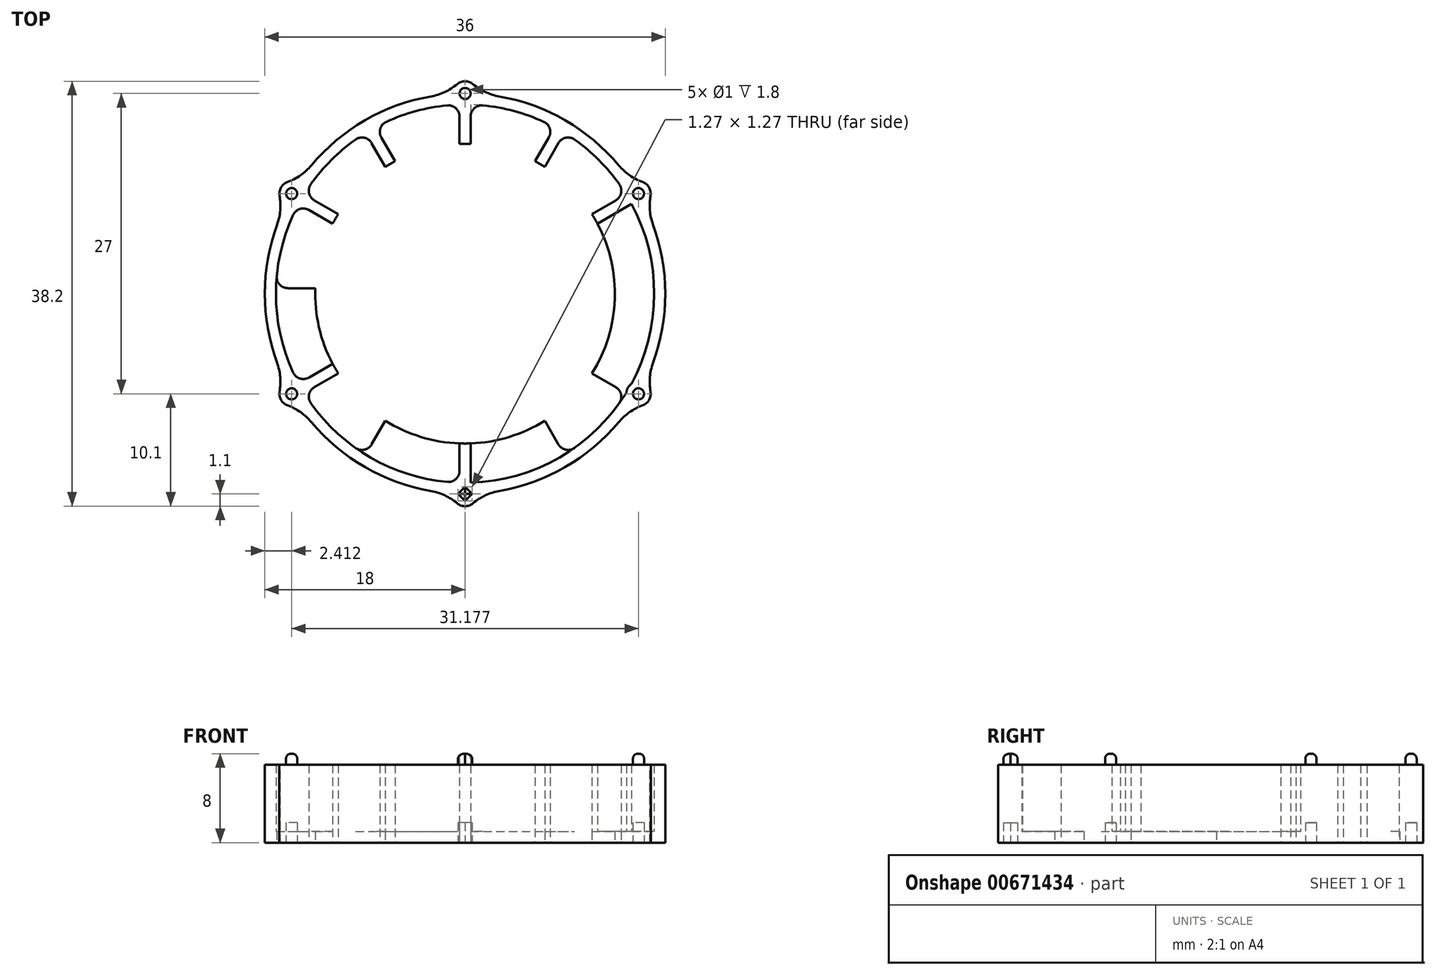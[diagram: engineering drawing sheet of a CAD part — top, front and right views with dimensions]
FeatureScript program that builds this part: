
annotation { "Feature Type Name" : "Feature", "Feature Type Description" : "" }
export const myFeature = defineFeature(function(context is Context, id is Id, definition is map)
    precondition{}
    {
        {
            var Q0;
            Q0=qCreatedBy(makeId("Top.planeOp"),FACE);
            var sketch = newSketch(context, id + "F0", { "sketchPlane" : qUnion([Q0])});
            skCircle(sketch, "E0", {"center": v(0, 0) * mm, "radius": 18 * mm});
            skCircle(sketch, "E1.0", {"center": v(0, 0) * mm, "radius": 17 * mm});
            skLineSegment(sketch, "E2.bottom", {"start": v(8.56, 15.83) * mm, "end": v(9.43, 15.33) * mm});
            skLineSegment(sketch, "E2.top", {"start": v(-9.43, -15.33) * mm, "end": v(-8.56, -15.83) * mm});
            skLineSegment(sketch, "E2.left", {"start": v(8.56, 15.83) * mm, "end": v(-9.43, -15.33) * mm});
            skLineSegment(sketch, "E2.right", {"start": v(9.43, 15.33) * mm, "end": v(-8.56, -15.83) * mm});
            skLineSegment(sketch, "E3.bottom", {"start": v(15.33, 9.43) * mm, "end": v(15.83, 8.56) * mm});
            skLineSegment(sketch, "E3.top", {"start": v(-15.83, -8.56) * mm, "end": v(-15.33, -9.43) * mm});
            skLineSegment(sketch, "E3.left", {"start": v(15.33, 9.43) * mm, "end": v(-15.83, -8.56) * mm});
            skLineSegment(sketch, "E3.right", {"start": v(15.83, 8.56) * mm, "end": v(-15.33, -9.43) * mm});
            skLineSegment(sketch, "E4", {"start": v(-38.35, 0) * mm, "end": v(39.17, 0) * mm, "construction": true});
            skLineSegment(sketch, "E5", {"start": v(0, 42.5) * mm, "end": v(0, -42.47) * mm, "construction": true});
            skLineSegment(sketch, "E6.bottom", {"start": v(-18, 0.5) * mm, "end": v(18, 0.5) * mm});
            skLineSegment(sketch, "E6.top", {"start": v(-18, -0.5) * mm, "end": v(18, -0.5) * mm});
            skLineSegment(sketch, "E6.left", {"start": v(-18, 0.5) * mm, "end": v(-18, -0.5) * mm});
            skLineSegment(sketch, "E6.right", {"start": v(18, 0.5) * mm, "end": v(18, -0.5) * mm});
            skLineSegment(sketch, "E7.bottom", {"start": v(-15.33, 9.43) * mm, "end": v(15.83, -8.56) * mm});
            skLineSegment(sketch, "E7.top", {"start": v(-15.83, 8.56) * mm, "end": v(15.33, -9.43) * mm});
            skLineSegment(sketch, "E7.left", {"start": v(-15.33, 9.43) * mm, "end": v(-15.83, 8.56) * mm});
            skLineSegment(sketch, "E7.right", {"start": v(15.83, -8.56) * mm, "end": v(15.33, -9.43) * mm});
            skLineSegment(sketch, "E8.bottom", {"start": v(-0.5, 18) * mm, "end": v(0.5, 18) * mm});
            skLineSegment(sketch, "E8.top", {"start": v(-0.5, -18) * mm, "end": v(0.5, -18) * mm});
            skLineSegment(sketch, "E8.left", {"start": v(-0.5, 18) * mm, "end": v(-0.5, -18) * mm});
            skLineSegment(sketch, "E8.right", {"start": v(0.5, 18) * mm, "end": v(0.5, -18) * mm});
            skLineSegment(sketch, "E9.bottom", {"start": v(-9.43, 15.33) * mm, "end": v(-8.56, 15.83) * mm});
            skLineSegment(sketch, "E9.top", {"start": v(8.56, -15.83) * mm, "end": v(9.43, -15.33) * mm});
            skLineSegment(sketch, "E9.left", {"start": v(-9.43, 15.33) * mm, "end": v(8.56, -15.83) * mm});
            skLineSegment(sketch, "E9.right", {"start": v(-8.56, 15.83) * mm, "end": v(9.43, -15.33) * mm});
            skCircle(sketch, "E10", {"center": v(0, 0) * mm, "radius": 13.47 * mm});
            skSolve(sketch);
        }
        {
            var Q0;
            Q0=qCreatedBy(makeId("Top.planeOp"),FACE);
            var sketch = newSketch(context, id + "F1", { "sketchPlane" : qUnion([Q0])});
            skCircle(sketch, "E11", {"center": v(0, 0) * mm, "radius": 18 * mm});
            skCircle(sketch, "E12", {"center": v(0, 0) * mm, "radius": 17 * mm});
            skSolve(sketch);
        }
        {
            var Q0;
            Q0=makeQuery(id+"F1.imprint","IMPRINT",FACE,{"disambiguationData":[TD([[makeQuery(id+"F1.imprint","IMPRINT",EDGE,{"derivedFrom":sQuery(id+"F1.wireOp",EDGE,"E11")}),1.0]])]});
            extrude(context, id + "F2", {"entities" : qUnion([Q0]), "depth" : 7 * mm, "offsetDistance" : 25 * mm});
        }
        {
            var Q0;
            {var subQ0=sQuery(id+"F0.wireOp",EDGE,"E7.bottom");var subQ1=sQuery(id+"F0.wireOp",EDGE,"E1.0");var subQ2=makeQuery(id+"F0.imprint","INTERSECT",VERTEX,{"disambiguationData":[OD(0.0)],"derivedFrom":[subQ1,subQ0]});Q0=makeQuery(id+"F0.imprint","IMPRINT",FACE,{"disambiguationData":[TD([[makeQuery(id+"F0.imprint","IMPRINT",EDGE,{"disambiguationData":[TD([[subQ2,-1.0]])],"derivedFrom":subQ1}),1.0]])]});}
            var Q1;
            {var subQ0=sQuery(id+"F0.wireOp",EDGE,"E2.right");var subQ1=sQuery(id+"F0.wireOp",EDGE,"E1.0");var subQ2=makeQuery(id+"F0.imprint","INTERSECT",VERTEX,{"disambiguationData":[OD(0.0)],"derivedFrom":[subQ1,subQ0]});Q1=makeQuery(id+"F0.imprint","IMPRINT",FACE,{"disambiguationData":[TD([[makeQuery(id+"F0.imprint","IMPRINT",EDGE,{"disambiguationData":[TD([[subQ2,-1.0]])],"derivedFrom":subQ1}),1.0]])]});}
            var Q2;
            {var subQ0=sQuery(id+"F0.wireOp",EDGE,"E8.left");var subQ1=sQuery(id+"F0.wireOp",EDGE,"E1.0");var subQ2=makeQuery(id+"F0.imprint","INTERSECT",VERTEX,{"disambiguationData":[OD(1.0)],"derivedFrom":[subQ1,subQ0]});Q2=makeQuery(id+"F0.imprint","IMPRINT",FACE,{"disambiguationData":[TD([[makeQuery(id+"F0.imprint","IMPRINT",EDGE,{"disambiguationData":[TD([[subQ2,-1.0]])],"derivedFrom":subQ1}),1.0]])]});}
            var Q3;
            {var subQ0=sQuery(id+"F0.wireOp",EDGE,"E3.left");var subQ1=sQuery(id+"F0.wireOp",EDGE,"E1.0");var subQ2=makeQuery(id+"F0.imprint","INTERSECT",VERTEX,{"disambiguationData":[OD(1.0)],"derivedFrom":[subQ1,subQ0]});Q3=makeQuery(id+"F0.imprint","IMPRINT",FACE,{"disambiguationData":[TD([[makeQuery(id+"F0.imprint","IMPRINT",EDGE,{"disambiguationData":[TD([[subQ2,-1.0]])],"derivedFrom":subQ1}),1.0]])]});}
            var Q4;
            {var subQ0=sQuery(id+"F0.wireOp",EDGE,"E9.right");var subQ1=sQuery(id+"F0.wireOp",EDGE,"E1.0");var subQ2=makeQuery(id+"F0.imprint","INTERSECT",VERTEX,{"disambiguationData":[OD(0.0)],"derivedFrom":[subQ1,subQ0]});Q4=makeQuery(id+"F0.imprint","IMPRINT",FACE,{"disambiguationData":[TD([[makeQuery(id+"F0.imprint","IMPRINT",EDGE,{"disambiguationData":[TD([[subQ2,-1.0]])],"derivedFrom":subQ1}),1.0]])]});}
            var Q5;
            {var subQ0=sQuery(id+"F0.wireOp",EDGE,"E8.right");var subQ1=sQuery(id+"F0.wireOp",EDGE,"E1.0");var subQ2=makeQuery(id+"F0.imprint","INTERSECT",VERTEX,{"disambiguationData":[OD(0.0)],"derivedFrom":[subQ1,subQ0]});Q5=makeQuery(id+"F0.imprint","IMPRINT",FACE,{"disambiguationData":[TD([[makeQuery(id+"F0.imprint","IMPRINT",EDGE,{"disambiguationData":[TD([[subQ2,-1.0]])],"derivedFrom":subQ1}),1.0]])]});}
            var Q6;
            {var subQ0=sQuery(id+"F0.wireOp",EDGE,"E3.right");var subQ1=sQuery(id+"F0.wireOp",EDGE,"E1.0");var subQ2=makeQuery(id+"F0.imprint","INTERSECT",VERTEX,{"disambiguationData":[OD(0.0)],"derivedFrom":[subQ1,subQ0]});Q6=makeQuery(id+"F0.imprint","IMPRINT",FACE,{"disambiguationData":[TD([[makeQuery(id+"F0.imprint","IMPRINT",EDGE,{"disambiguationData":[TD([[subQ2,-1.0]])],"derivedFrom":subQ1}),1.0]])]});}
            extrude(context, id + "F3", {"entities" : qUnion([Q0, Q1, Q2, Q3, Q4, Q5, Q6]), "operationType" : NewBodyOperationType.ADD, "depth" : 7 * mm, "offsetDistance" : 25 * mm});
        }
        {
            var Q0;
            Q0=makeQuery(id+"F1.imprint","IMPRINT",FACE,{"disambiguationData":[TD([[makeQuery(id+"F1.imprint","IMPRINT",EDGE,{"derivedFrom":sQuery(id+"F1.wireOp",EDGE,"E11")}),1.0]])]});
            var Q1;
            Q1=makeQuery(id+"F1.imprint","IMPRINT",FACE,{"disambiguationData":[TD([[makeQuery(id+"F1.imprint","IMPRINT",EDGE,{"derivedFrom":sQuery(id+"F1.wireOp",EDGE,"E12")}),1.0]])]});
            extrude(context, id + "F4", {"entities" : qUnion([Q0, Q1]), "operationType" : NewBodyOperationType.ADD, "depth" : 1 * mm, "offsetDistance" : 25 * mm});
        }
        {
            var Q0;
            Q0=qCreatedBy(makeId("Top.planeOp"),FACE);
            var sketch = newSketch(context, id + "F5", { "sketchPlane" : qUnion([Q0])});
            skCircle(sketch, "E13", {"center": v(0, 0) * mm, "radius": 18 * mm});
            skLineSegment(sketch, "E14", {"start": v(0, 18) * mm, "end": v(0, -18) * mm, "construction": true});
            skLineSegment(sketch, "E15", {"start": v(15.59, 9) * mm, "end": v(0, 0) * mm, "construction": true});
            skLineSegment(sketch, "E16", {"start": v(9, 15.59) * mm, "end": v(0, 0) * mm, "construction": true});
            skLineSegment(sketch, "E17", {"start": v(0, 0) * mm, "end": v(18, 0) * mm, "construction": true});
            skLineSegment(sketch, "E18", {"start": v(0, 0) * mm, "end": v(15.59, -9) * mm, "construction": true});
            skLineSegment(sketch, "E19", {"start": v(0, 0) * mm, "end": v(9, -15.59) * mm, "construction": true});
            skLineSegment(sketch, "E20", {"start": v(0, 0) * mm, "end": v(-9, 15.59) * mm, "construction": true});
            skLineSegment(sketch, "E21", {"start": v(0, 0) * mm, "end": v(-15.59, 9) * mm, "construction": true});
            skLineSegment(sketch, "E22", {"start": v(0, 0) * mm, "end": v(-18, 0) * mm, "construction": true});
            skLineSegment(sketch, "E23", {"start": v(0, 0) * mm, "end": v(-15.59, -9) * mm, "construction": true});
            skLineSegment(sketch, "E24", {"start": v(0, 0) * mm, "end": v(-9, -15.59) * mm, "construction": true});
            skCircle(sketch, "E25", {"center": v(0, 18) * mm, "radius": 1.1 * mm});
            skCircle(sketch, "E26", {"center": v(15.59, 9) * mm, "radius": 1.1 * mm});
            skCircle(sketch, "E27", {"center": v(15.59, -9) * mm, "radius": 1.1 * mm});
            skCircle(sketch, "E28", {"center": v(0, -18) * mm, "radius": 1.1 * mm});
            skCircle(sketch, "E29", {"center": v(-15.59, -9) * mm, "radius": 1.1 * mm});
            skCircle(sketch, "E30", {"center": v(-15.59, 9) * mm, "radius": 1.1 * mm});
            skCircle(sketch, "E31", {"center": v(-15.59, 9) * mm, "radius": 0.5 * mm});
            skCircle(sketch, "E32", {"center": v(0, 18) * mm, "radius": 0.5 * mm});
            skCircle(sketch, "E33", {"center": v(15.59, 9) * mm, "radius": 0.5 * mm});
            skCircle(sketch, "E34", {"center": v(15.59, -9) * mm, "radius": 0.5 * mm});
            skCircle(sketch, "E35", {"center": v(-15.59, -9) * mm, "radius": 0.5 * mm});
            skLineSegment(sketch, "E36.bottom", {"start": v(0.64, -18) * mm, "end": v(0, -18.64) * mm});
            skLineSegment(sketch, "E36.top", {"start": v(0, -17.36) * mm, "end": v(-0.64, -18) * mm});
            skLineSegment(sketch, "E36.left", {"start": v(0.64, -18) * mm, "end": v(0, -17.36) * mm});
            skLineSegment(sketch, "E36.right", {"start": v(0, -18.64) * mm, "end": v(-0.64, -18) * mm});
            skSolve(sketch);
        }
        {
            var Q0;
            {var subQ0=sQuery(id+"F5.wireOp",EDGE,"E30");var subQ1=sQuery(id+"F5.wireOp",EDGE,"E13");var subQ2=makeQuery(id+"F5.imprint","INTERSECT",VERTEX,{"disambiguationData":[OD(0.0)],"derivedFrom":[subQ1,subQ0]});Q0=makeQuery(id+"F5.imprint","IMPRINT",FACE,{"disambiguationData":[TD([[makeQuery(id+"F5.imprint","IMPRINT",EDGE,{"disambiguationData":[TD([[subQ2,-1.0]])],"derivedFrom":subQ1}),1.0]])]});}
            var Q1;
            {var subQ0=sQuery(id+"F5.wireOp",EDGE,"E30");var subQ1=sQuery(id+"F5.wireOp",EDGE,"E13");var subQ2=makeQuery(id+"F5.imprint","INTERSECT",VERTEX,{"disambiguationData":[OD(0.0)],"derivedFrom":[subQ1,subQ0]});Q1=makeQuery(id+"F5.imprint","IMPRINT",FACE,{"disambiguationData":[TD([[makeQuery(id+"F5.imprint","IMPRINT",EDGE,{"disambiguationData":[TD([[subQ2,-1.0]])],"derivedFrom":subQ1}),-1.0]])]});}
            var Q2;
            {var subQ0=sQuery(id+"F5.wireOp",EDGE,"E25");var subQ1=sQuery(id+"F5.wireOp",EDGE,"E13");var subQ2=makeQuery(id+"F5.imprint","INTERSECT",VERTEX,{"disambiguationData":[OD(0.0)],"derivedFrom":[subQ1,subQ0]});Q2=makeQuery(id+"F5.imprint","IMPRINT",FACE,{"disambiguationData":[TD([[makeQuery(id+"F5.imprint","IMPRINT",EDGE,{"disambiguationData":[TD([[subQ2,-1.0]])],"derivedFrom":subQ1}),1.0]])]});}
            var Q3;
            {var subQ0=sQuery(id+"F5.wireOp",EDGE,"E25");var subQ1=sQuery(id+"F5.wireOp",EDGE,"E13");var subQ2=makeQuery(id+"F5.imprint","INTERSECT",VERTEX,{"disambiguationData":[OD(0.0)],"derivedFrom":[subQ1,subQ0]});Q3=makeQuery(id+"F5.imprint","IMPRINT",FACE,{"disambiguationData":[TD([[makeQuery(id+"F5.imprint","IMPRINT",EDGE,{"disambiguationData":[TD([[subQ2,-1.0]])],"derivedFrom":subQ1}),-1.0]])]});}
            var Q4;
            {var subQ0=sQuery(id+"F5.wireOp",EDGE,"E26");var subQ1=sQuery(id+"F5.wireOp",EDGE,"E13");var subQ2=makeQuery(id+"F5.imprint","INTERSECT",VERTEX,{"disambiguationData":[OD(0.0)],"derivedFrom":[subQ1,subQ0]});Q4=makeQuery(id+"F5.imprint","IMPRINT",FACE,{"disambiguationData":[TD([[makeQuery(id+"F5.imprint","IMPRINT",EDGE,{"disambiguationData":[TD([[subQ2,-1.0]])],"derivedFrom":subQ1}),-1.0]])]});}
            var Q5;
            {var subQ0=sQuery(id+"F5.wireOp",EDGE,"E26");var subQ1=sQuery(id+"F5.wireOp",EDGE,"E13");var subQ2=makeQuery(id+"F5.imprint","INTERSECT",VERTEX,{"disambiguationData":[OD(0.0)],"derivedFrom":[subQ1,subQ0]});Q5=makeQuery(id+"F5.imprint","IMPRINT",FACE,{"disambiguationData":[TD([[makeQuery(id+"F5.imprint","IMPRINT",EDGE,{"disambiguationData":[TD([[subQ2,-1.0]])],"derivedFrom":subQ1}),1.0]])]});}
            var Q6;
            {var subQ0=sQuery(id+"F5.wireOp",EDGE,"E29");var subQ1=sQuery(id+"F5.wireOp",EDGE,"E13");var subQ2=makeQuery(id+"F5.imprint","INTERSECT",VERTEX,{"disambiguationData":[OD(0.0)],"derivedFrom":[subQ1,subQ0]});Q6=makeQuery(id+"F5.imprint","IMPRINT",FACE,{"disambiguationData":[TD([[makeQuery(id+"F5.imprint","IMPRINT",EDGE,{"disambiguationData":[TD([[subQ2,-1.0]])],"derivedFrom":subQ1}),1.0]])]});}
            var Q7;
            {var subQ0=sQuery(id+"F5.wireOp",EDGE,"E29");var subQ1=sQuery(id+"F5.wireOp",EDGE,"E13");var subQ2=makeQuery(id+"F5.imprint","INTERSECT",VERTEX,{"disambiguationData":[OD(0.0)],"derivedFrom":[subQ1,subQ0]});Q7=makeQuery(id+"F5.imprint","IMPRINT",FACE,{"disambiguationData":[TD([[makeQuery(id+"F5.imprint","IMPRINT",EDGE,{"disambiguationData":[TD([[subQ2,-1.0]])],"derivedFrom":subQ1}),-1.0]])]});}
            var Q8;
            {var subQ3=sQuery(id+"F5.wireOp",EDGE,"E13");var subQ5=sQuery(id+"F5.wireOp",EDGE,"E28");var subQ6=makeQuery(id+"F5.imprint","INTERSECT",VERTEX,{"disambiguationData":[OD(0.0)],"derivedFrom":[subQ3,subQ5]});Q8=makeQuery(id+"F5.imprint","IMPRINT",FACE,{"disambiguationData":[TD([[makeQuery(id+"F5.imprint","IMPRINT",EDGE,{"disambiguationData":[TD([[subQ6,-1.0]])],"derivedFrom":subQ3}),1.0]])]});}
            var Q9;
            {var subQ6=sQuery(id+"F5.wireOp",EDGE,"E36.bottom");Q9=makeQuery(id+"F5.imprint","IMPRINT",FACE,{"disambiguationData":[TD([[makeQuery(id+"F5.imprint","IMPRINT",EDGE,{"derivedFrom":subQ6}),1.0]])]});}
            var Q10;
            {var subQ0=sQuery(id+"F5.wireOp",EDGE,"E27");var subQ1=sQuery(id+"F5.wireOp",EDGE,"E13");var subQ2=makeQuery(id+"F5.imprint","INTERSECT",VERTEX,{"disambiguationData":[OD(0.0)],"derivedFrom":[subQ1,subQ0]});Q10=makeQuery(id+"F5.imprint","IMPRINT",FACE,{"disambiguationData":[TD([[makeQuery(id+"F5.imprint","IMPRINT",EDGE,{"disambiguationData":[TD([[subQ2,-1.0]])],"derivedFrom":subQ1}),-1.0]])]});}
            var Q11;
            {var subQ0=sQuery(id+"F5.wireOp",EDGE,"E27");var subQ1=sQuery(id+"F5.wireOp",EDGE,"E13");var subQ2=makeQuery(id+"F5.imprint","INTERSECT",VERTEX,{"disambiguationData":[OD(0.0)],"derivedFrom":[subQ1,subQ0]});Q11=makeQuery(id+"F5.imprint","IMPRINT",FACE,{"disambiguationData":[TD([[makeQuery(id+"F5.imprint","IMPRINT",EDGE,{"disambiguationData":[TD([[subQ2,-1.0]])],"derivedFrom":subQ1}),1.0]])]});}
            var Q12;
            {var subQ0=sQuery(id+"F5.wireOp",EDGE,"E31");var subQ1=sQuery(id+"F5.wireOp",EDGE,"E13");var subQ2=makeQuery(id+"F5.imprint","INTERSECT",VERTEX,{"disambiguationData":[OD(0.0)],"derivedFrom":[subQ1,subQ0]});Q12=makeQuery(id+"F5.imprint","IMPRINT",FACE,{"disambiguationData":[TD([[makeQuery(id+"F5.imprint","IMPRINT",EDGE,{"disambiguationData":[TD([[subQ2,-1.0]])],"derivedFrom":subQ1}),1.0]])]});}
            var Q13;
            {var subQ0=sQuery(id+"F5.wireOp",EDGE,"E31");var subQ1=sQuery(id+"F5.wireOp",EDGE,"E13");var subQ2=makeQuery(id+"F5.imprint","INTERSECT",VERTEX,{"disambiguationData":[OD(0.0)],"derivedFrom":[subQ1,subQ0]});Q13=makeQuery(id+"F5.imprint","IMPRINT",FACE,{"disambiguationData":[TD([[makeQuery(id+"F5.imprint","IMPRINT",EDGE,{"disambiguationData":[TD([[subQ2,-1.0]])],"derivedFrom":subQ1}),-1.0]])]});}
            var Q14;
            {var subQ0=sQuery(id+"F5.wireOp",EDGE,"E32");var subQ1=sQuery(id+"F5.wireOp",EDGE,"E13");var subQ2=makeQuery(id+"F5.imprint","INTERSECT",VERTEX,{"disambiguationData":[OD(0.0)],"derivedFrom":[subQ1,subQ0]});Q14=makeQuery(id+"F5.imprint","IMPRINT",FACE,{"disambiguationData":[TD([[makeQuery(id+"F5.imprint","IMPRINT",EDGE,{"disambiguationData":[TD([[subQ2,-1.0]])],"derivedFrom":subQ1}),-1.0]])]});}
            var Q15;
            {var subQ0=sQuery(id+"F5.wireOp",EDGE,"E32");var subQ1=sQuery(id+"F5.wireOp",EDGE,"E13");var subQ2=makeQuery(id+"F5.imprint","INTERSECT",VERTEX,{"disambiguationData":[OD(0.0)],"derivedFrom":[subQ1,subQ0]});Q15=makeQuery(id+"F5.imprint","IMPRINT",FACE,{"disambiguationData":[TD([[makeQuery(id+"F5.imprint","IMPRINT",EDGE,{"disambiguationData":[TD([[subQ2,-1.0]])],"derivedFrom":subQ1}),1.0]])]});}
            var Q16;
            {var subQ0=sQuery(id+"F5.wireOp",EDGE,"E33");var subQ1=sQuery(id+"F5.wireOp",EDGE,"E13");var subQ2=makeQuery(id+"F5.imprint","INTERSECT",VERTEX,{"disambiguationData":[OD(0.0)],"derivedFrom":[subQ1,subQ0]});Q16=makeQuery(id+"F5.imprint","IMPRINT",FACE,{"disambiguationData":[TD([[makeQuery(id+"F5.imprint","IMPRINT",EDGE,{"disambiguationData":[TD([[subQ2,-1.0]])],"derivedFrom":subQ1}),-1.0]])]});}
            var Q17;
            {var subQ0=sQuery(id+"F5.wireOp",EDGE,"E33");var subQ1=sQuery(id+"F5.wireOp",EDGE,"E13");var subQ2=makeQuery(id+"F5.imprint","INTERSECT",VERTEX,{"disambiguationData":[OD(0.0)],"derivedFrom":[subQ1,subQ0]});Q17=makeQuery(id+"F5.imprint","IMPRINT",FACE,{"disambiguationData":[TD([[makeQuery(id+"F5.imprint","IMPRINT",EDGE,{"disambiguationData":[TD([[subQ2,-1.0]])],"derivedFrom":subQ1}),1.0]])]});}
            var Q18;
            {var subQ0=sQuery(id+"F5.wireOp",EDGE,"E34");var subQ1=sQuery(id+"F5.wireOp",EDGE,"E13");var subQ2=makeQuery(id+"F5.imprint","INTERSECT",VERTEX,{"disambiguationData":[OD(0.0)],"derivedFrom":[subQ1,subQ0]});Q18=makeQuery(id+"F5.imprint","IMPRINT",FACE,{"disambiguationData":[TD([[makeQuery(id+"F5.imprint","IMPRINT",EDGE,{"disambiguationData":[TD([[subQ2,-1.0]])],"derivedFrom":subQ1}),-1.0]])]});}
            var Q19;
            {var subQ0=sQuery(id+"F5.wireOp",EDGE,"E34");var subQ1=sQuery(id+"F5.wireOp",EDGE,"E13");var subQ2=makeQuery(id+"F5.imprint","INTERSECT",VERTEX,{"disambiguationData":[OD(0.0)],"derivedFrom":[subQ1,subQ0]});Q19=makeQuery(id+"F5.imprint","IMPRINT",FACE,{"disambiguationData":[TD([[makeQuery(id+"F5.imprint","IMPRINT",EDGE,{"disambiguationData":[TD([[subQ2,-1.0]])],"derivedFrom":subQ1}),1.0]])]});}
            var Q20;
            {var subQ1=sQuery(id+"F5.wireOp",EDGE,"E36.bottom");Q20=makeQuery(id+"F5.imprint","IMPRINT",FACE,{"disambiguationData":[TD([[makeQuery(id+"F5.imprint","IMPRINT",EDGE,{"derivedFrom":subQ1}),-1.0]])]});}
            var Q21;
            {var subQ0=sQuery(id+"F5.wireOp",EDGE,"E35");var subQ1=sQuery(id+"F5.wireOp",EDGE,"E13");var subQ2=makeQuery(id+"F5.imprint","INTERSECT",VERTEX,{"disambiguationData":[OD(0.0)],"derivedFrom":[subQ1,subQ0]});Q21=makeQuery(id+"F5.imprint","IMPRINT",FACE,{"disambiguationData":[TD([[makeQuery(id+"F5.imprint","IMPRINT",EDGE,{"disambiguationData":[TD([[subQ2,-1.0]])],"derivedFrom":subQ1}),-1.0]])]});}
            var Q22;
            {var subQ0=sQuery(id+"F5.wireOp",EDGE,"E35");var subQ1=sQuery(id+"F5.wireOp",EDGE,"E13");var subQ2=makeQuery(id+"F5.imprint","INTERSECT",VERTEX,{"disambiguationData":[OD(0.0)],"derivedFrom":[subQ1,subQ0]});Q22=makeQuery(id+"F5.imprint","IMPRINT",FACE,{"disambiguationData":[TD([[makeQuery(id+"F5.imprint","IMPRINT",EDGE,{"disambiguationData":[TD([[subQ2,-1.0]])],"derivedFrom":subQ1}),1.0]])]});}
            var Q23;
            {var subQ0=sQuery(id+"F5.wireOp",EDGE,"E36.top");var subQ1=sQuery(id+"F5.wireOp",EDGE,"E13");var subQ2=makeQuery(id+"F5.imprint","INTERSECT",VERTEX,{"derivedFrom":[subQ1,subQ0]});Q23=makeQuery(id+"F5.imprint","IMPRINT",FACE,{"disambiguationData":[TD([[makeQuery(id+"F5.imprint","IMPRINT",EDGE,{"disambiguationData":[TD([[subQ2,-1.0]])],"derivedFrom":subQ1}),1.0]])]});}
            extrude(context, id + "F6", {"entities" : qUnion([Q0, Q1, Q2, Q3, Q4, Q5, Q6, Q7, Q8, Q9, Q10, Q11, Q12, Q13, Q14, Q15, Q16, Q17, Q18, Q19, Q20, Q21, Q22, Q23]), "operationType" : NewBodyOperationType.ADD, "depth" : 7 * mm, "offsetDistance" : 25 * mm});
        }
        {
            var Q0;
            {var subQ0=sQuery(id+"F0.wireOp",EDGE,"E8.right");var subQ1=sQuery(id+"F0.wireOp",EDGE,"E1.0");Q0=makeQuery(id+"F3.opExtrude","SWEPT_EDGE",EDGE,{"disambiguationData":[OSD([subQ1,subQ0]),TDD([makeQuery(id+"F0.imprint","INTERSECT",VERTEX,{"disambiguationData":[OD(1.0)],"derivedFrom":[subQ1,subQ0]})])]});}
            var Q1;
            {var subQ0=sQuery(id+"F0.wireOp",EDGE,"E2.left");var subQ1=sQuery(id+"F0.wireOp",EDGE,"E1.0");Q1=makeQuery(id+"F3.opExtrude","SWEPT_EDGE",EDGE,{"disambiguationData":[OSD([subQ1,subQ0]),TDD([makeQuery(id+"F0.imprint","INTERSECT",VERTEX,{"disambiguationData":[OD(1.0)],"derivedFrom":[subQ1,subQ0]})])]});}
            var Q2;
            {var subQ0=sQuery(id+"F0.wireOp",EDGE,"E3.left");var subQ1=sQuery(id+"F0.wireOp",EDGE,"E1.0");Q2=makeQuery(id+"F3.opExtrude","SWEPT_EDGE",EDGE,{"disambiguationData":[OSD([subQ1,subQ0]),TDD([makeQuery(id+"F0.imprint","INTERSECT",VERTEX,{"disambiguationData":[OD(1.0)],"derivedFrom":[subQ1,subQ0]})])]});}
            var Q3;
            {var subQ0=sQuery(id+"F0.wireOp",EDGE,"E6.bottom");var subQ1=sQuery(id+"F0.wireOp",EDGE,"E1.0");Q3=makeQuery(id+"F3.opExtrude","SWEPT_EDGE",EDGE,{"disambiguationData":[OSD([subQ1,subQ0]),TDD([makeQuery(id+"F0.imprint","INTERSECT",VERTEX,{"disambiguationData":[OD(1.0)],"derivedFrom":[subQ1,subQ0]})])]});}
            var Q4;
            {var subQ0=sQuery(id+"F0.wireOp",EDGE,"E9.right");var subQ1=sQuery(id+"F0.wireOp",EDGE,"E1.0");Q4=makeQuery(id+"F3.opExtrude","SWEPT_EDGE",EDGE,{"disambiguationData":[OSD([subQ1,subQ0]),TDD([makeQuery(id+"F0.imprint","INTERSECT",VERTEX,{"disambiguationData":[OD(1.0)],"derivedFrom":[subQ1,subQ0]})])]});}
            var Q5;
            {var subQ0=sQuery(id+"F0.wireOp",EDGE,"E7.bottom");var subQ1=sQuery(id+"F0.wireOp",EDGE,"E1.0");Q5=makeQuery(id+"F3.opExtrude","SWEPT_EDGE",EDGE,{"disambiguationData":[OSD([subQ1,subQ0]),TDD([makeQuery(id+"F0.imprint","INTERSECT",VERTEX,{"disambiguationData":[OD(1.0)],"derivedFrom":[subQ1,subQ0]})])]});}
            var Q6;
            {var subQ0=sQuery(id+"F0.wireOp",EDGE,"E8.left");var subQ1=sQuery(id+"F0.wireOp",EDGE,"E1.0");Q6=makeQuery(id+"F3.opExtrude","SWEPT_EDGE",EDGE,{"disambiguationData":[OSD([subQ1,subQ0]),TDD([makeQuery(id+"F0.imprint","INTERSECT",VERTEX,{"disambiguationData":[OD(0.0)],"derivedFrom":[subQ1,subQ0]})])]});}
            var Q7;
            {var subQ0=sQuery(id+"F0.wireOp",EDGE,"E2.left");var subQ1=sQuery(id+"F0.wireOp",EDGE,"E1.0");Q7=makeQuery(id+"F3.opExtrude","SWEPT_EDGE",EDGE,{"disambiguationData":[OSD([subQ1,subQ0]),TDD([makeQuery(id+"F0.imprint","INTERSECT",VERTEX,{"disambiguationData":[OD(0.0)],"derivedFrom":[subQ1,subQ0]})])]});}
            var Q8;
            {var subQ0=sQuery(id+"F0.wireOp",EDGE,"E3.left");var subQ1=sQuery(id+"F0.wireOp",EDGE,"E1.0");Q8=makeQuery(id+"F3.opExtrude","SWEPT_EDGE",EDGE,{"disambiguationData":[OSD([subQ1,subQ0]),TDD([makeQuery(id+"F0.imprint","INTERSECT",VERTEX,{"disambiguationData":[OD(0.0)],"derivedFrom":[subQ1,subQ0]})])]});}
            var Q9;
            {var subQ0=sQuery(id+"F0.wireOp",EDGE,"E6.top");var subQ1=sQuery(id+"F0.wireOp",EDGE,"E1.0");Q9=makeQuery(id+"F3.opExtrude","SWEPT_EDGE",EDGE,{"disambiguationData":[OSD([subQ1,subQ0]),TDD([makeQuery(id+"F0.imprint","INTERSECT",VERTEX,{"disambiguationData":[OD(1.0)],"derivedFrom":[subQ1,subQ0]})])]});}
            var Q10;
            {var subQ0=sQuery(id+"F0.wireOp",EDGE,"E7.top");var subQ1=sQuery(id+"F0.wireOp",EDGE,"E1.0");Q10=makeQuery(id+"F3.opExtrude","SWEPT_EDGE",EDGE,{"disambiguationData":[OSD([subQ1,subQ0]),TDD([makeQuery(id+"F0.imprint","INTERSECT",VERTEX,{"disambiguationData":[OD(0.0)],"derivedFrom":[subQ1,subQ0]})])]});}
            var Q11;
            {var subQ0=sQuery(id+"F0.wireOp",EDGE,"E6.top");var subQ1=sQuery(id+"F0.wireOp",EDGE,"E1.0");Q11=makeQuery(id+"F3.opExtrude","SWEPT_EDGE",EDGE,{"disambiguationData":[OSD([subQ1,subQ0]),TDD([makeQuery(id+"F0.imprint","INTERSECT",VERTEX,{"disambiguationData":[OD(0.0)],"derivedFrom":[subQ1,subQ0]})])]});}
            var Q12;
            {var subQ0=sQuery(id+"F0.wireOp",EDGE,"E9.left");var subQ1=sQuery(id+"F0.wireOp",EDGE,"E1.0");Q12=makeQuery(id+"F3.opExtrude","SWEPT_EDGE",EDGE,{"disambiguationData":[OSD([subQ1,subQ0]),TDD([makeQuery(id+"F0.imprint","INTERSECT",VERTEX,{"disambiguationData":[OD(0.0)],"derivedFrom":[subQ1,subQ0]})])]});}
            var Q13;
            {var subQ0=sQuery(id+"F0.wireOp",EDGE,"E8.right");var subQ1=sQuery(id+"F0.wireOp",EDGE,"E1.0");Q13=makeQuery(id+"F3.opExtrude","SWEPT_EDGE",EDGE,{"disambiguationData":[OSD([subQ1,subQ0]),TDD([makeQuery(id+"F0.imprint","INTERSECT",VERTEX,{"disambiguationData":[OD(0.0)],"derivedFrom":[subQ1,subQ0]})])]});}
            var Q14;
            {var subQ0=sQuery(id+"F0.wireOp",EDGE,"E7.bottom");var subQ1=sQuery(id+"F0.wireOp",EDGE,"E1.0");Q14=makeQuery(id+"F3.opExtrude","SWEPT_EDGE",EDGE,{"disambiguationData":[OSD([subQ1,subQ0]),TDD([makeQuery(id+"F0.imprint","INTERSECT",VERTEX,{"disambiguationData":[OD(0.0)],"derivedFrom":[subQ1,subQ0]})])]});}
            var Q15;
            {var subQ0=sQuery(id+"F0.wireOp",EDGE,"E9.right");var subQ1=sQuery(id+"F0.wireOp",EDGE,"E1.0");Q15=makeQuery(id+"F3.opExtrude","SWEPT_EDGE",EDGE,{"disambiguationData":[OSD([subQ1,subQ0]),TDD([makeQuery(id+"F0.imprint","INTERSECT",VERTEX,{"disambiguationData":[OD(0.0)],"derivedFrom":[subQ1,subQ0]})])]});}
            var Q16;
            {var subQ0=sQuery(id+"F0.wireOp",EDGE,"E3.right");var subQ1=sQuery(id+"F0.wireOp",EDGE,"E1.0");Q16=makeQuery(id+"F3.opExtrude","SWEPT_EDGE",EDGE,{"disambiguationData":[OSD([subQ1,subQ0]),TDD([makeQuery(id+"F0.imprint","INTERSECT",VERTEX,{"disambiguationData":[OD(1.0)],"derivedFrom":[subQ1,subQ0]})])]});}
            var Q17;
            {var subQ0=sQuery(id+"F0.wireOp",EDGE,"E2.right");var subQ1=sQuery(id+"F0.wireOp",EDGE,"E1.0");Q17=makeQuery(id+"F3.opExtrude","SWEPT_EDGE",EDGE,{"disambiguationData":[OSD([subQ1,subQ0]),TDD([makeQuery(id+"F0.imprint","INTERSECT",VERTEX,{"disambiguationData":[OD(1.0)],"derivedFrom":[subQ1,subQ0]})])]});}
            var Q18;
            {var subQ0=sQuery(id+"F0.wireOp",EDGE,"E3.right");var subQ1=sQuery(id+"F0.wireOp",EDGE,"E1.0");Q18=makeQuery(id+"F3.opExtrude","SWEPT_EDGE",EDGE,{"disambiguationData":[OSD([subQ1,subQ0]),TDD([makeQuery(id+"F0.imprint","INTERSECT",VERTEX,{"disambiguationData":[OD(0.0)],"derivedFrom":[subQ1,subQ0]})])]});}
            var Q19;
            {var subQ0=sQuery(id+"F0.wireOp",EDGE,"E2.right");var subQ1=sQuery(id+"F0.wireOp",EDGE,"E1.0");Q19=makeQuery(id+"F3.opExtrude","SWEPT_EDGE",EDGE,{"disambiguationData":[OSD([subQ1,subQ0]),TDD([makeQuery(id+"F0.imprint","INTERSECT",VERTEX,{"disambiguationData":[OD(0.0)],"derivedFrom":[subQ1,subQ0]})])]});}
            var Q20;
            {var subQ0=sQuery(id+"F0.wireOp",EDGE,"E8.left");var subQ1=sQuery(id+"F0.wireOp",EDGE,"E1.0");Q20=makeQuery(id+"F3.opExtrude","SWEPT_EDGE",EDGE,{"disambiguationData":[OSD([subQ1,subQ0]),TDD([makeQuery(id+"F0.imprint","INTERSECT",VERTEX,{"disambiguationData":[OD(1.0)],"derivedFrom":[subQ1,subQ0]})])]});}
            var Q21;
            {var subQ0=sQuery(id+"F0.wireOp",EDGE,"E9.left");var subQ1=sQuery(id+"F0.wireOp",EDGE,"E1.0");Q21=makeQuery(id+"F3.opExtrude","SWEPT_EDGE",EDGE,{"disambiguationData":[OSD([subQ1,subQ0]),TDD([makeQuery(id+"F0.imprint","INTERSECT",VERTEX,{"disambiguationData":[OD(1.0)],"derivedFrom":[subQ1,subQ0]})])]});}
            var Q22;
            {var subQ0=sQuery(id+"F0.wireOp",EDGE,"E7.top");var subQ1=sQuery(id+"F0.wireOp",EDGE,"E1.0");Q22=makeQuery(id+"F3.opExtrude","SWEPT_EDGE",EDGE,{"disambiguationData":[OSD([subQ1,subQ0]),TDD([makeQuery(id+"F0.imprint","INTERSECT",VERTEX,{"disambiguationData":[OD(1.0)],"derivedFrom":[subQ1,subQ0]})])]});}
            var Q23;
            {var subQ0=sQuery(id+"F0.wireOp",EDGE,"E6.bottom");var subQ1=sQuery(id+"F0.wireOp",EDGE,"E1.0");Q23=makeQuery(id+"F3.opExtrude","SWEPT_EDGE",EDGE,{"disambiguationData":[OSD([subQ1,subQ0]),TDD([makeQuery(id+"F0.imprint","INTERSECT",VERTEX,{"disambiguationData":[OD(0.0)],"derivedFrom":[subQ1,subQ0]})])]});}
            fillet(context, id + "F7", {"entities" : qUnion([Q0, Q1, Q2, Q3, Q4, Q5, Q6, Q7, Q8, Q9, Q10, Q11, Q12, Q13, Q14, Q15, Q16, Q17, Q18, Q19, Q20, Q21, Q22, Q23]), "radius" : 1 * mm, "tangentPropagation" : true, "allowEdgeOverflow" : false});
        }
        {
            var Q0;
            Q0=makeQuery(id+"F6.boolean.opBoolean","INTERSECT",EDGE,{"disambiguationData":[OD(0.0)],"derivedFrom":[makeQuery(id+"F2.opExtrude","SWEPT_FACE",FACE,{"disambiguationData":[OSD([sQuery(id+"F1.wireOp",EDGE,"E11")])]}),makeQuery(id+"F6.opExtrude","SWEPT_FACE",FACE,{"disambiguationData":[OSD([sQuery(id+"F5.wireOp",EDGE,"E30")])]})]});
            var Q1;
            Q1=makeQuery(id+"F6.boolean.opBoolean","INTERSECT",EDGE,{"disambiguationData":[OD(1.0)],"derivedFrom":[makeQuery(id+"F2.opExtrude","SWEPT_FACE",FACE,{"disambiguationData":[OSD([sQuery(id+"F1.wireOp",EDGE,"E11")])]}),makeQuery(id+"F6.opExtrude","SWEPT_FACE",FACE,{"disambiguationData":[OSD([sQuery(id+"F5.wireOp",EDGE,"E30")])]})]});
            var Q2;
            Q2=makeQuery(id+"F6.boolean.opBoolean","INTERSECT",EDGE,{"disambiguationData":[OD(1.0)],"derivedFrom":[makeQuery(id+"F2.opExtrude","SWEPT_FACE",FACE,{"disambiguationData":[OSD([sQuery(id+"F1.wireOp",EDGE,"E11")])]}),makeQuery(id+"F6.opExtrude","SWEPT_FACE",FACE,{"disambiguationData":[OSD([sQuery(id+"F5.wireOp",EDGE,"E25")])]})]});
            var Q3;
            Q3=makeQuery(id+"F6.boolean.opBoolean","INTERSECT",EDGE,{"disambiguationData":[OD(1.0)],"derivedFrom":[makeQuery(id+"F2.opExtrude","SWEPT_FACE",FACE,{"disambiguationData":[OSD([sQuery(id+"F1.wireOp",EDGE,"E11")])]}),makeQuery(id+"F6.opExtrude","SWEPT_FACE",FACE,{"disambiguationData":[OSD([sQuery(id+"F5.wireOp",EDGE,"E29")])]})]});
            var Q4;
            Q4=makeQuery(id+"F6.boolean.opBoolean","INTERSECT",EDGE,{"disambiguationData":[OD(0.0)],"derivedFrom":[makeQuery(id+"F2.opExtrude","SWEPT_FACE",FACE,{"disambiguationData":[OSD([sQuery(id+"F1.wireOp",EDGE,"E11")])]}),makeQuery(id+"F6.opExtrude","SWEPT_FACE",FACE,{"disambiguationData":[OSD([sQuery(id+"F5.wireOp",EDGE,"E29")])]})]});
            var Q5;
            Q5=makeQuery(id+"F6.boolean.opBoolean","INTERSECT",EDGE,{"disambiguationData":[OD(1.0)],"derivedFrom":[makeQuery(id+"F2.opExtrude","SWEPT_FACE",FACE,{"disambiguationData":[OSD([sQuery(id+"F1.wireOp",EDGE,"E11")])]}),makeQuery(id+"F6.opExtrude","SWEPT_FACE",FACE,{"disambiguationData":[OSD([sQuery(id+"F5.wireOp",EDGE,"E28")])]})]});
            var Q6;
            Q6=makeQuery(id+"F6.boolean.opBoolean","INTERSECT",EDGE,{"disambiguationData":[OD(0.0)],"derivedFrom":[makeQuery(id+"F2.opExtrude","SWEPT_FACE",FACE,{"disambiguationData":[OSD([sQuery(id+"F1.wireOp",EDGE,"E11")])]}),makeQuery(id+"F6.opExtrude","SWEPT_FACE",FACE,{"disambiguationData":[OSD([sQuery(id+"F5.wireOp",EDGE,"E28")])]})]});
            var Q7;
            Q7=makeQuery(id+"F6.boolean.opBoolean","INTERSECT",EDGE,{"disambiguationData":[OD(1.0)],"derivedFrom":[makeQuery(id+"F2.opExtrude","SWEPT_FACE",FACE,{"disambiguationData":[OSD([sQuery(id+"F1.wireOp",EDGE,"E11")])]}),makeQuery(id+"F6.opExtrude","SWEPT_FACE",FACE,{"disambiguationData":[OSD([sQuery(id+"F5.wireOp",EDGE,"E27")])]})]});
            var Q8;
            Q8=makeQuery(id+"F6.boolean.opBoolean","INTERSECT",EDGE,{"disambiguationData":[OD(0.0)],"derivedFrom":[makeQuery(id+"F2.opExtrude","SWEPT_FACE",FACE,{"disambiguationData":[OSD([sQuery(id+"F1.wireOp",EDGE,"E11")])]}),makeQuery(id+"F6.opExtrude","SWEPT_FACE",FACE,{"disambiguationData":[OSD([sQuery(id+"F5.wireOp",EDGE,"E27")])]})]});
            var Q9;
            Q9=makeQuery(id+"F6.boolean.opBoolean","INTERSECT",EDGE,{"disambiguationData":[OD(1.0)],"derivedFrom":[makeQuery(id+"F2.opExtrude","SWEPT_FACE",FACE,{"disambiguationData":[OSD([sQuery(id+"F1.wireOp",EDGE,"E11")])]}),makeQuery(id+"F6.opExtrude","SWEPT_FACE",FACE,{"disambiguationData":[OSD([sQuery(id+"F5.wireOp",EDGE,"E26")])]})]});
            var Q10;
            Q10=makeQuery(id+"F6.boolean.opBoolean","INTERSECT",EDGE,{"disambiguationData":[OD(0.0)],"derivedFrom":[makeQuery(id+"F2.opExtrude","SWEPT_FACE",FACE,{"disambiguationData":[OSD([sQuery(id+"F1.wireOp",EDGE,"E11")])]}),makeQuery(id+"F6.opExtrude","SWEPT_FACE",FACE,{"disambiguationData":[OSD([sQuery(id+"F5.wireOp",EDGE,"E26")])]})]});
            var Q11;
            Q11=makeQuery(id+"F6.boolean.opBoolean","INTERSECT",EDGE,{"disambiguationData":[OD(0.0)],"derivedFrom":[makeQuery(id+"F2.opExtrude","SWEPT_FACE",FACE,{"disambiguationData":[OSD([sQuery(id+"F1.wireOp",EDGE,"E11")])]}),makeQuery(id+"F6.opExtrude","SWEPT_FACE",FACE,{"disambiguationData":[OSD([sQuery(id+"F5.wireOp",EDGE,"E25")])]})]});
            fillet(context, id + "F8", {"entities" : qUnion([Q0, Q1, Q2, Q3, Q4, Q5, Q6, Q7, Q8, Q9, Q10, Q11]), "radius" : 5 * mm, "tangentPropagation" : true, "allowEdgeOverflow" : false});
        }
        {
            var Q0;
            {var subQ0=sQuery(id+"F5.wireOp",EDGE,"E31");var subQ1=sQuery(id+"F5.wireOp",EDGE,"E13");var subQ2=makeQuery(id+"F5.imprint","INTERSECT",VERTEX,{"disambiguationData":[OD(0.0)],"derivedFrom":[subQ1,subQ0]});Q0=makeQuery(id+"F5.imprint","IMPRINT",FACE,{"disambiguationData":[TD([[makeQuery(id+"F5.imprint","IMPRINT",EDGE,{"disambiguationData":[TD([[subQ2,-1.0]])],"derivedFrom":subQ1}),-1.0]])]});}
            var Q1;
            {var subQ0=sQuery(id+"F5.wireOp",EDGE,"E31");var subQ1=sQuery(id+"F5.wireOp",EDGE,"E13");var subQ2=makeQuery(id+"F5.imprint","INTERSECT",VERTEX,{"disambiguationData":[OD(0.0)],"derivedFrom":[subQ1,subQ0]});Q1=makeQuery(id+"F5.imprint","IMPRINT",FACE,{"disambiguationData":[TD([[makeQuery(id+"F5.imprint","IMPRINT",EDGE,{"disambiguationData":[TD([[subQ2,-1.0]])],"derivedFrom":subQ1}),1.0]])]});}
            var Q2;
            {var subQ0=sQuery(id+"F5.wireOp",EDGE,"E32");var subQ1=sQuery(id+"F5.wireOp",EDGE,"E13");var subQ2=makeQuery(id+"F5.imprint","INTERSECT",VERTEX,{"disambiguationData":[OD(0.0)],"derivedFrom":[subQ1,subQ0]});Q2=makeQuery(id+"F5.imprint","IMPRINT",FACE,{"disambiguationData":[TD([[makeQuery(id+"F5.imprint","IMPRINT",EDGE,{"disambiguationData":[TD([[subQ2,-1.0]])],"derivedFrom":subQ1}),-1.0]])]});}
            var Q3;
            {var subQ0=sQuery(id+"F5.wireOp",EDGE,"E32");var subQ1=sQuery(id+"F5.wireOp",EDGE,"E13");var subQ2=makeQuery(id+"F5.imprint","INTERSECT",VERTEX,{"disambiguationData":[OD(0.0)],"derivedFrom":[subQ1,subQ0]});Q3=makeQuery(id+"F5.imprint","IMPRINT",FACE,{"disambiguationData":[TD([[makeQuery(id+"F5.imprint","IMPRINT",EDGE,{"disambiguationData":[TD([[subQ2,-1.0]])],"derivedFrom":subQ1}),1.0]])]});}
            var Q4;
            {var subQ0=sQuery(id+"F5.wireOp",EDGE,"E33");var subQ1=sQuery(id+"F5.wireOp",EDGE,"E13");var subQ2=makeQuery(id+"F5.imprint","INTERSECT",VERTEX,{"disambiguationData":[OD(0.0)],"derivedFrom":[subQ1,subQ0]});Q4=makeQuery(id+"F5.imprint","IMPRINT",FACE,{"disambiguationData":[TD([[makeQuery(id+"F5.imprint","IMPRINT",EDGE,{"disambiguationData":[TD([[subQ2,-1.0]])],"derivedFrom":subQ1}),1.0]])]});}
            var Q5;
            {var subQ0=sQuery(id+"F5.wireOp",EDGE,"E33");var subQ1=sQuery(id+"F5.wireOp",EDGE,"E13");var subQ2=makeQuery(id+"F5.imprint","INTERSECT",VERTEX,{"disambiguationData":[OD(0.0)],"derivedFrom":[subQ1,subQ0]});Q5=makeQuery(id+"F5.imprint","IMPRINT",FACE,{"disambiguationData":[TD([[makeQuery(id+"F5.imprint","IMPRINT",EDGE,{"disambiguationData":[TD([[subQ2,-1.0]])],"derivedFrom":subQ1}),-1.0]])]});}
            var Q6;
            {var subQ0=sQuery(id+"F5.wireOp",EDGE,"E34");var subQ1=sQuery(id+"F5.wireOp",EDGE,"E13");var subQ2=makeQuery(id+"F5.imprint","INTERSECT",VERTEX,{"disambiguationData":[OD(0.0)],"derivedFrom":[subQ1,subQ0]});Q6=makeQuery(id+"F5.imprint","IMPRINT",FACE,{"disambiguationData":[TD([[makeQuery(id+"F5.imprint","IMPRINT",EDGE,{"disambiguationData":[TD([[subQ2,-1.0]])],"derivedFrom":subQ1}),1.0]])]});}
            var Q7;
            {var subQ0=sQuery(id+"F5.wireOp",EDGE,"E34");var subQ1=sQuery(id+"F5.wireOp",EDGE,"E13");var subQ2=makeQuery(id+"F5.imprint","INTERSECT",VERTEX,{"disambiguationData":[OD(0.0)],"derivedFrom":[subQ1,subQ0]});Q7=makeQuery(id+"F5.imprint","IMPRINT",FACE,{"disambiguationData":[TD([[makeQuery(id+"F5.imprint","IMPRINT",EDGE,{"disambiguationData":[TD([[subQ2,-1.0]])],"derivedFrom":subQ1}),-1.0]])]});}
            var Q8;
            {var subQ1=sQuery(id+"F5.wireOp",EDGE,"E36.bottom");Q8=makeQuery(id+"F5.imprint","IMPRINT",FACE,{"disambiguationData":[TD([[makeQuery(id+"F5.imprint","IMPRINT",EDGE,{"derivedFrom":subQ1}),-1.0]])]});}
            var Q9;
            {var subQ0=sQuery(id+"F5.wireOp",EDGE,"E36.top");var subQ1=sQuery(id+"F5.wireOp",EDGE,"E13");var subQ2=makeQuery(id+"F5.imprint","INTERSECT",VERTEX,{"derivedFrom":[subQ1,subQ0]});Q9=makeQuery(id+"F5.imprint","IMPRINT",FACE,{"disambiguationData":[TD([[makeQuery(id+"F5.imprint","IMPRINT",EDGE,{"disambiguationData":[TD([[subQ2,-1.0]])],"derivedFrom":subQ1}),1.0]])]});}
            var Q10;
            {var subQ0=sQuery(id+"F5.wireOp",EDGE,"E35");var subQ1=sQuery(id+"F5.wireOp",EDGE,"E13");var subQ2=makeQuery(id+"F5.imprint","INTERSECT",VERTEX,{"disambiguationData":[OD(0.0)],"derivedFrom":[subQ1,subQ0]});Q10=makeQuery(id+"F5.imprint","IMPRINT",FACE,{"disambiguationData":[TD([[makeQuery(id+"F5.imprint","IMPRINT",EDGE,{"disambiguationData":[TD([[subQ2,-1.0]])],"derivedFrom":subQ1}),-1.0]])]});}
            var Q11;
            {var subQ0=sQuery(id+"F5.wireOp",EDGE,"E35");var subQ1=sQuery(id+"F5.wireOp",EDGE,"E13");var subQ2=makeQuery(id+"F5.imprint","INTERSECT",VERTEX,{"disambiguationData":[OD(0.0)],"derivedFrom":[subQ1,subQ0]});Q11=makeQuery(id+"F5.imprint","IMPRINT",FACE,{"disambiguationData":[TD([[makeQuery(id+"F5.imprint","IMPRINT",EDGE,{"disambiguationData":[TD([[subQ2,-1.0]])],"derivedFrom":subQ1}),1.0]])]});}
            extrude(context, id + "F9", {"entities" : qUnion([Q0, Q1, Q2, Q3, Q4, Q5, Q6, Q7, Q8, Q9, Q10, Q11]), "operationType" : NewBodyOperationType.ADD, "depth" : 8 * mm, "offsetDistance" : 25 * mm});
        }
        {
            var Q0;
            Q0=makeQuery(id+"F9.opExtrude","CAP_EDGE",EDGE,{"disambiguationData":[OSD([sQuery(id+"F5.wireOp",EDGE,"E35")])],"isStart":false});
            var Q1;
            Q1=makeQuery(id+"F9.opExtrude","CAP_FACE",FACE,{"disambiguationData":[OSD([sQuery(id+"F5.wireOp",EDGE,"E31")])],"isStart":false});
            var Q2;
            Q2=makeQuery(id+"F9.opExtrude","CAP_FACE",FACE,{"disambiguationData":[OSD([sQuery(id+"F5.wireOp",EDGE,"E32")])],"isStart":false});
            var Q3;
            Q3=makeQuery(id+"F9.opExtrude","CAP_FACE",FACE,{"disambiguationData":[OSD([sQuery(id+"F5.wireOp",EDGE,"E33")])],"isStart":false});
            var Q4;
            Q4=makeQuery(id+"F9.opExtrude","CAP_FACE",FACE,{"disambiguationData":[OSD([sQuery(id+"F5.wireOp",EDGE,"E34")])],"isStart":false});
            var Q5;
            Q5=makeQuery(id+"F9.opExtrude","CAP_EDGE",EDGE,{"disambiguationData":[OSD([sQuery(id+"F5.wireOp",EDGE,"E36.left")])],"isStart":false});
            var Q6;
            Q6=makeQuery(id+"F9.opExtrude","CAP_EDGE",EDGE,{"disambiguationData":[OSD([sQuery(id+"F5.wireOp",EDGE,"E36.right")])],"isStart":false});
            var Q7;
            Q7=makeQuery(id+"F9.opExtrude","CAP_EDGE",EDGE,{"disambiguationData":[OSD([sQuery(id+"F5.wireOp",EDGE,"E36.bottom")])],"isStart":false});
            var Q8;
            Q8=makeQuery(id+"F9.opExtrude","CAP_EDGE",EDGE,{"disambiguationData":[OSD([sQuery(id+"F5.wireOp",EDGE,"E36.top")])],"isStart":false});
            fillet(context, id + "F10", {"entities" : qUnion([Q0, Q1, Q2, Q3, Q4, Q5, Q6, Q7, Q8]), "radius" : .45 * mm, "tangentPropagation" : true, "allowEdgeOverflow" : false});
        }
        {
            var Q0;
            {var subQ0=sQuery(id+"F5.wireOp",EDGE,"E35");var subQ1=sQuery(id+"F5.wireOp",EDGE,"E13");var subQ2=makeQuery(id+"F5.imprint","INTERSECT",VERTEX,{"disambiguationData":[OD(0.0)],"derivedFrom":[subQ1,subQ0]});Q0=makeQuery(id+"F5.imprint","IMPRINT",FACE,{"disambiguationData":[TD([[makeQuery(id+"F5.imprint","IMPRINT",EDGE,{"disambiguationData":[TD([[subQ2,-1.0]])],"derivedFrom":subQ1}),-1.0]])]});}
            var Q1;
            {var subQ0=sQuery(id+"F5.wireOp",EDGE,"E35");var subQ1=sQuery(id+"F5.wireOp",EDGE,"E13");var subQ2=makeQuery(id+"F5.imprint","INTERSECT",VERTEX,{"disambiguationData":[OD(0.0)],"derivedFrom":[subQ1,subQ0]});Q1=makeQuery(id+"F5.imprint","IMPRINT",FACE,{"disambiguationData":[TD([[makeQuery(id+"F5.imprint","IMPRINT",EDGE,{"disambiguationData":[TD([[subQ2,-1.0]])],"derivedFrom":subQ1}),1.0]])]});}
            var Q2;
            {var subQ1=sQuery(id+"F5.wireOp",EDGE,"E36.bottom");Q2=makeQuery(id+"F5.imprint","IMPRINT",FACE,{"disambiguationData":[TD([[makeQuery(id+"F5.imprint","IMPRINT",EDGE,{"derivedFrom":subQ1}),-1.0]])]});}
            var Q3;
            {var subQ0=sQuery(id+"F5.wireOp",EDGE,"E36.top");var subQ1=sQuery(id+"F5.wireOp",EDGE,"E13");var subQ2=makeQuery(id+"F5.imprint","INTERSECT",VERTEX,{"derivedFrom":[subQ1,subQ0]});Q3=makeQuery(id+"F5.imprint","IMPRINT",FACE,{"disambiguationData":[TD([[makeQuery(id+"F5.imprint","IMPRINT",EDGE,{"disambiguationData":[TD([[subQ2,-1.0]])],"derivedFrom":subQ1}),1.0]])]});}
            var Q4;
            {var subQ0=sQuery(id+"F5.wireOp",EDGE,"E34");var subQ1=sQuery(id+"F5.wireOp",EDGE,"E13");var subQ2=makeQuery(id+"F5.imprint","INTERSECT",VERTEX,{"disambiguationData":[OD(0.0)],"derivedFrom":[subQ1,subQ0]});Q4=makeQuery(id+"F5.imprint","IMPRINT",FACE,{"disambiguationData":[TD([[makeQuery(id+"F5.imprint","IMPRINT",EDGE,{"disambiguationData":[TD([[subQ2,-1.0]])],"derivedFrom":subQ1}),1.0]])]});}
            var Q5;
            {var subQ0=sQuery(id+"F5.wireOp",EDGE,"E34");var subQ1=sQuery(id+"F5.wireOp",EDGE,"E13");var subQ2=makeQuery(id+"F5.imprint","INTERSECT",VERTEX,{"disambiguationData":[OD(0.0)],"derivedFrom":[subQ1,subQ0]});Q5=makeQuery(id+"F5.imprint","IMPRINT",FACE,{"disambiguationData":[TD([[makeQuery(id+"F5.imprint","IMPRINT",EDGE,{"disambiguationData":[TD([[subQ2,-1.0]])],"derivedFrom":subQ1}),-1.0]])]});}
            var Q6;
            {var subQ0=sQuery(id+"F5.wireOp",EDGE,"E33");var subQ1=sQuery(id+"F5.wireOp",EDGE,"E13");var subQ2=makeQuery(id+"F5.imprint","INTERSECT",VERTEX,{"disambiguationData":[OD(0.0)],"derivedFrom":[subQ1,subQ0]});Q6=makeQuery(id+"F5.imprint","IMPRINT",FACE,{"disambiguationData":[TD([[makeQuery(id+"F5.imprint","IMPRINT",EDGE,{"disambiguationData":[TD([[subQ2,-1.0]])],"derivedFrom":subQ1}),1.0]])]});}
            var Q7;
            {var subQ0=sQuery(id+"F5.wireOp",EDGE,"E33");var subQ1=sQuery(id+"F5.wireOp",EDGE,"E13");var subQ2=makeQuery(id+"F5.imprint","INTERSECT",VERTEX,{"disambiguationData":[OD(0.0)],"derivedFrom":[subQ1,subQ0]});Q7=makeQuery(id+"F5.imprint","IMPRINT",FACE,{"disambiguationData":[TD([[makeQuery(id+"F5.imprint","IMPRINT",EDGE,{"disambiguationData":[TD([[subQ2,-1.0]])],"derivedFrom":subQ1}),-1.0]])]});}
            var Q8;
            {var subQ0=sQuery(id+"F5.wireOp",EDGE,"E32");var subQ1=sQuery(id+"F5.wireOp",EDGE,"E13");var subQ2=makeQuery(id+"F5.imprint","INTERSECT",VERTEX,{"disambiguationData":[OD(0.0)],"derivedFrom":[subQ1,subQ0]});Q8=makeQuery(id+"F5.imprint","IMPRINT",FACE,{"disambiguationData":[TD([[makeQuery(id+"F5.imprint","IMPRINT",EDGE,{"disambiguationData":[TD([[subQ2,-1.0]])],"derivedFrom":subQ1}),1.0]])]});}
            var Q9;
            {var subQ0=sQuery(id+"F5.wireOp",EDGE,"E32");var subQ1=sQuery(id+"F5.wireOp",EDGE,"E13");var subQ2=makeQuery(id+"F5.imprint","INTERSECT",VERTEX,{"disambiguationData":[OD(0.0)],"derivedFrom":[subQ1,subQ0]});Q9=makeQuery(id+"F5.imprint","IMPRINT",FACE,{"disambiguationData":[TD([[makeQuery(id+"F5.imprint","IMPRINT",EDGE,{"disambiguationData":[TD([[subQ2,-1.0]])],"derivedFrom":subQ1}),-1.0]])]});}
            var Q10;
            {var subQ0=sQuery(id+"F5.wireOp",EDGE,"E31");var subQ1=sQuery(id+"F5.wireOp",EDGE,"E13");var subQ2=makeQuery(id+"F5.imprint","INTERSECT",VERTEX,{"disambiguationData":[OD(0.0)],"derivedFrom":[subQ1,subQ0]});Q10=makeQuery(id+"F5.imprint","IMPRINT",FACE,{"disambiguationData":[TD([[makeQuery(id+"F5.imprint","IMPRINT",EDGE,{"disambiguationData":[TD([[subQ2,-1.0]])],"derivedFrom":subQ1}),-1.0]])]});}
            var Q11;
            {var subQ0=sQuery(id+"F5.wireOp",EDGE,"E31");var subQ1=sQuery(id+"F5.wireOp",EDGE,"E13");var subQ2=makeQuery(id+"F5.imprint","INTERSECT",VERTEX,{"disambiguationData":[OD(0.0)],"derivedFrom":[subQ1,subQ0]});Q11=makeQuery(id+"F5.imprint","IMPRINT",FACE,{"disambiguationData":[TD([[makeQuery(id+"F5.imprint","IMPRINT",EDGE,{"disambiguationData":[TD([[subQ2,-1.0]])],"derivedFrom":subQ1}),1.0]])]});}
            extrude(context, id + "F11", {"entities" : qUnion([Q0, Q1, Q2, Q3, Q4, Q5, Q6, Q7, Q8, Q9, Q10, Q11]), "operationType" : NewBodyOperationType.REMOVE, "depth" : 1.8 * mm, "offsetDistance" : 25 * mm});
        }
        {
            var Q0;
            Q0=qCreatedBy(makeId("Top.planeOp"),FACE);
            var sketch = newSketch(context, id + "F12", { "sketchPlane" : qUnion([Q0])});
            skCircle(sketch, "E37", {"center": v(0, 0) * mm, "radius": 13.47 * mm});
            skSolve(sketch);
        }
        {
            var Q0;
            Q0=makeQuery(id+"F12.imprint","IMPRINT",FACE,{"disambiguationData":[TD([[makeQuery(id+"F12.imprint","IMPRINT",EDGE,{"derivedFrom":sQuery(id+"F12.wireOp",EDGE,"E37")}),1.0]])]});
            extrude(context, id + "F13", {"entities" : qUnion([Q0]), "operationType" : NewBodyOperationType.REMOVE, "depth" : 1 * mm, "offsetDistance" : 25 * mm});
        }
        {
            var Q0;
            {var subQ0=sQuery(id+"F0.wireOp",EDGE,"E9.right");var subQ1=sQuery(id+"F0.wireOp",EDGE,"E1.0");var subQ2=makeQuery(id+"F0.imprint","INTERSECT",VERTEX,{"disambiguationData":[OD(1.0)],"derivedFrom":[subQ1,subQ0]});Q0=makeQuery(id+"F0.imprint","IMPRINT",FACE,{"disambiguationData":[TD([[makeQuery(id+"F0.imprint","IMPRINT",EDGE,{"disambiguationData":[TD([[subQ2,-1.0]])],"derivedFrom":subQ1}),1.0]])]});}
            var Q1;
            {var subQ0=sQuery(id+"F0.wireOp",EDGE,"E3.left");var subQ1=sQuery(id+"F0.wireOp",EDGE,"E1.0");var subQ2=makeQuery(id+"F0.imprint","INTERSECT",VERTEX,{"disambiguationData":[OD(0.0)],"derivedFrom":[subQ1,subQ0]});Q1=makeQuery(id+"F0.imprint","IMPRINT",FACE,{"disambiguationData":[TD([[makeQuery(id+"F0.imprint","IMPRINT",EDGE,{"disambiguationData":[TD([[subQ2,-1.0]])],"derivedFrom":subQ1}),1.0]])]});}
            var Q2;
            {var subQ0=sQuery(id+"F0.wireOp",EDGE,"E2.left");var subQ1=sQuery(id+"F0.wireOp",EDGE,"E1.0");var subQ2=makeQuery(id+"F0.imprint","INTERSECT",VERTEX,{"disambiguationData":[OD(0.0)],"derivedFrom":[subQ1,subQ0]});Q2=makeQuery(id+"F0.imprint","IMPRINT",FACE,{"disambiguationData":[TD([[makeQuery(id+"F0.imprint","IMPRINT",EDGE,{"disambiguationData":[TD([[subQ2,-1.0]])],"derivedFrom":subQ1}),1.0]])]});}
            var Q3;
            {var subQ0=sQuery(id+"F0.wireOp",EDGE,"E8.left");var subQ1=sQuery(id+"F0.wireOp",EDGE,"E1.0");var subQ2=makeQuery(id+"F0.imprint","INTERSECT",VERTEX,{"disambiguationData":[OD(0.0)],"derivedFrom":[subQ1,subQ0]});Q3=makeQuery(id+"F0.imprint","IMPRINT",FACE,{"disambiguationData":[TD([[makeQuery(id+"F0.imprint","IMPRINT",EDGE,{"disambiguationData":[TD([[subQ2,-1.0]])],"derivedFrom":subQ1}),1.0]])]});}
            var Q4;
            {var subQ0=sQuery(id+"F0.wireOp",EDGE,"E9.left");var subQ1=sQuery(id+"F0.wireOp",EDGE,"E1.0");var subQ2=makeQuery(id+"F0.imprint","INTERSECT",VERTEX,{"disambiguationData":[OD(0.0)],"derivedFrom":[subQ1,subQ0]});Q4=makeQuery(id+"F0.imprint","IMPRINT",FACE,{"disambiguationData":[TD([[makeQuery(id+"F0.imprint","IMPRINT",EDGE,{"disambiguationData":[TD([[subQ2,-1.0]])],"derivedFrom":subQ1}),1.0]])]});}
            var Q5;
            {var subQ0=sQuery(id+"F0.wireOp",EDGE,"E7.top");var subQ1=sQuery(id+"F0.wireOp",EDGE,"E1.0");var subQ2=makeQuery(id+"F0.imprint","INTERSECT",VERTEX,{"disambiguationData":[OD(0.0)],"derivedFrom":[subQ1,subQ0]});Q5=makeQuery(id+"F0.imprint","IMPRINT",FACE,{"disambiguationData":[TD([[makeQuery(id+"F0.imprint","IMPRINT",EDGE,{"disambiguationData":[TD([[subQ2,-1.0]])],"derivedFrom":subQ1}),1.0]])]});}
            var Q6;
            {var subQ0=sQuery(id+"F0.wireOp",EDGE,"E3.right");var subQ1=sQuery(id+"F0.wireOp",EDGE,"E1.0");var subQ2=makeQuery(id+"F0.imprint","INTERSECT",VERTEX,{"disambiguationData":[OD(1.0)],"derivedFrom":[subQ1,subQ0]});Q6=makeQuery(id+"F0.imprint","IMPRINT",FACE,{"disambiguationData":[TD([[makeQuery(id+"F0.imprint","IMPRINT",EDGE,{"disambiguationData":[TD([[subQ2,-1.0]])],"derivedFrom":subQ1}),1.0]])]});}
            extrude(context, id + "F14", {"entities" : qUnion([Q0, Q1, Q2, Q3, Q4, Q5, Q6]), "operationType" : NewBodyOperationType.REMOVE, "depth" : 1 * mm, "offsetDistance" : 25 * mm});
        }
        {
            var Q0;
            {var subQ0=sQuery(id+"F0.wireOp",EDGE,"E7.top");var subQ1=sQuery(id+"F0.wireOp",EDGE,"E1.0");Q0=makeQuery(id+"F14.boolean.opBoolean","COPY",EDGE,{"derivedFrom":makeQuery(id+"F14.opExtrude","SWEPT_EDGE",EDGE,{"disambiguationData":[OSD([subQ1,subQ0]),TDD([makeQuery(id+"F0.imprint","INTERSECT",VERTEX,{"disambiguationData":[OD(0.0)],"derivedFrom":[subQ1,subQ0]})])]})});}
            var Q1;
            Q1=makeQuery(id+"F14.boolean.opBoolean","COPY",EDGE,{"derivedFrom":makeQuery(id+"F14.opExtrude","SWEPT_EDGE",EDGE,{"disambiguationData":[OSD([sQuery(id+"F0.wireOp",EDGE,"E1.0"),sQuery(id+"F0.wireOp",EDGE,"E9.left")])]})});
            var Q2;
            Q2=makeQuery(id+"F14.boolean.opBoolean","COPY",EDGE,{"derivedFrom":makeQuery(id+"F14.opExtrude","SWEPT_EDGE",EDGE,{"disambiguationData":[OSD([sQuery(id+"F0.wireOp",EDGE,"E1.0"),sQuery(id+"F0.wireOp",EDGE,"E2.right")])]})});
            var Q3;
            Q3=makeQuery(id+"F14.boolean.opBoolean","COPY",EDGE,{"derivedFrom":makeQuery(id+"F14.opExtrude","SWEPT_EDGE",EDGE,{"disambiguationData":[OSD([sQuery(id+"F0.wireOp",EDGE,"E1.0"),sQuery(id+"F0.wireOp",EDGE,"E6.bottom")])]})});
            var Q4;
            {var subQ0=sQuery(id+"F0.wireOp",EDGE,"E2.left");var subQ1=sQuery(id+"F0.wireOp",EDGE,"E1.0");Q4=makeQuery(id+"F14.boolean.opBoolean","COPY",EDGE,{"derivedFrom":makeQuery(id+"F14.opExtrude","SWEPT_EDGE",EDGE,{"disambiguationData":[OSD([subQ1,subQ0]),TDD([makeQuery(id+"F0.imprint","INTERSECT",VERTEX,{"disambiguationData":[OD(1.0)],"derivedFrom":[subQ1,subQ0]})])]})});}
            var Q5;
            Q5=makeQuery(id+"F14.boolean.opBoolean","COPY",EDGE,{"derivedFrom":makeQuery(id+"F14.opExtrude","SWEPT_EDGE",EDGE,{"disambiguationData":[OSD([sQuery(id+"F0.wireOp",EDGE,"E1.0"),sQuery(id+"F0.wireOp",EDGE,"E7.bottom")])]})});
            var Q6;
            {var subQ0=sQuery(id+"F0.wireOp",EDGE,"E9.right");var subQ1=sQuery(id+"F0.wireOp",EDGE,"E1.0");Q6=makeQuery(id+"F14.boolean.opBoolean","COPY",EDGE,{"derivedFrom":makeQuery(id+"F14.opExtrude","SWEPT_EDGE",EDGE,{"disambiguationData":[OSD([subQ1,subQ0]),TDD([makeQuery(id+"F0.imprint","INTERSECT",VERTEX,{"disambiguationData":[OD(0.0)],"derivedFrom":[subQ1,subQ0]})])]})});}
            var Q7;
            Q7=makeQuery(id+"F14.boolean.opBoolean","COPY",EDGE,{"derivedFrom":makeQuery(id+"F14.opExtrude","SWEPT_EDGE",EDGE,{"disambiguationData":[OSD([sQuery(id+"F0.wireOp",EDGE,"E1.0"),sQuery(id+"F0.wireOp",EDGE,"E8.left")])]})});
            var Q8;
            {var subQ0=sQuery(id+"F0.wireOp",EDGE,"E2.left");var subQ1=sQuery(id+"F0.wireOp",EDGE,"E1.0");Q8=makeQuery(id+"F14.boolean.opBoolean","COPY",EDGE,{"derivedFrom":makeQuery(id+"F14.opExtrude","SWEPT_EDGE",EDGE,{"disambiguationData":[OSD([subQ1,subQ0]),TDD([makeQuery(id+"F0.imprint","INTERSECT",VERTEX,{"disambiguationData":[OD(0.0)],"derivedFrom":[subQ1,subQ0]})])]})});}
            var Q9;
            Q9=makeQuery(id+"F14.boolean.opBoolean","COPY",EDGE,{"derivedFrom":makeQuery(id+"F14.opExtrude","SWEPT_EDGE",EDGE,{"disambiguationData":[OSD([sQuery(id+"F0.wireOp",EDGE,"E1.0"),sQuery(id+"F0.wireOp",EDGE,"E3.left")])]})});
            var Q10;
            {var subQ0=sQuery(id+"F0.wireOp",EDGE,"E9.right");var subQ1=sQuery(id+"F0.wireOp",EDGE,"E1.0");Q10=makeQuery(id+"F14.boolean.opBoolean","COPY",EDGE,{"derivedFrom":makeQuery(id+"F14.opExtrude","SWEPT_EDGE",EDGE,{"disambiguationData":[OSD([subQ1,subQ0]),TDD([makeQuery(id+"F0.imprint","INTERSECT",VERTEX,{"disambiguationData":[OD(1.0)],"derivedFrom":[subQ1,subQ0]})])]})});}
            var Q11;
            {var subQ0=sQuery(id+"F0.wireOp",EDGE,"E7.top");var subQ1=sQuery(id+"F0.wireOp",EDGE,"E1.0");Q11=makeQuery(id+"F14.boolean.opBoolean","COPY",EDGE,{"derivedFrom":makeQuery(id+"F14.opExtrude","SWEPT_EDGE",EDGE,{"disambiguationData":[OSD([subQ1,subQ0]),TDD([makeQuery(id+"F0.imprint","INTERSECT",VERTEX,{"disambiguationData":[OD(1.0)],"derivedFrom":[subQ1,subQ0]})])]})});}
            var Q12;
            Q12=makeQuery(id+"F14.boolean.opBoolean","COPY",EDGE,{"derivedFrom":makeQuery(id+"F14.opExtrude","SWEPT_EDGE",EDGE,{"disambiguationData":[OSD([sQuery(id+"F0.wireOp",EDGE,"E1.0"),sQuery(id+"F0.wireOp",EDGE,"E3.right")])]})});
            fillet(context, id + "F15", {"entities" : qUnion([Q0, Q1, Q2, Q3, Q4, Q5, Q6, Q7, Q8, Q9, Q10, Q11, Q12]), "radius" : 1 * mm, "tangentPropagation" : true, "allowEdgeOverflow" : false});
        }
    });
